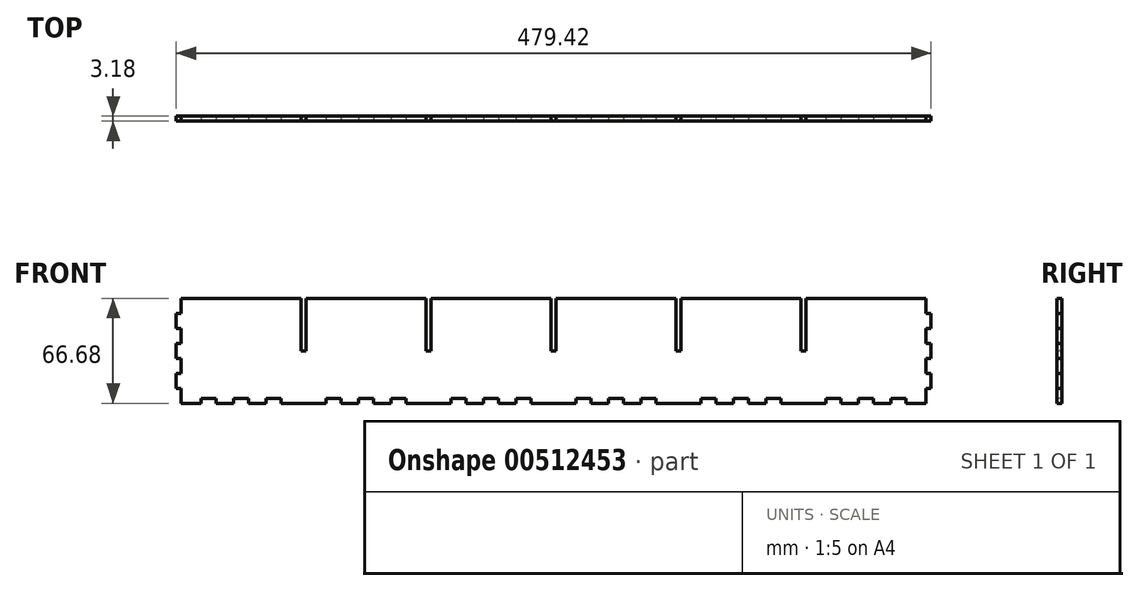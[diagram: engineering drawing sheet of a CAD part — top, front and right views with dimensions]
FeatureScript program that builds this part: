
annotation { "Feature Type Name" : "Feature", "Feature Type Description" : "" }
export const myFeature = defineFeature(function(context is Context, id is Id, definition is map)
    precondition{}
    {
        {
            var Q0;
            Q0=qCreatedBy(makeId("Front.planeOp"),FACE);
            var sketch = newSketch(context, id + "F0", { "sketchPlane" : qUnion([Q0])});
            skLineSegment(sketch, "E0.bottom", {"start": v(-239.71, 33.34) * mm, "end": v(239.71, 33.34) * mm});
            skLineSegment(sketch, "E0.top", {"start": v(-239.71, -33.34) * mm, "end": v(239.71, -33.34) * mm});
            skLineSegment(sketch, "E0.left", {"start": v(-239.71, 33.34) * mm, "end": v(-239.71, -33.34) * mm});
            skLineSegment(sketch, "E0.right", {"start": v(239.71, 33.34) * mm, "end": v(239.71, -33.34) * mm});
            skSolve(sketch);
        }
        {
            var Q0;
            Q0=makeQuery(id+"F0.imprint","IMPRINT",FACE,{"disambiguationData":[TD([[makeQuery(id+"F0.imprint","IMPRINT",EDGE,{"derivedFrom":sQuery(id+"F0.wireOp",EDGE,"E0.bottom")}),-1.0]])]});
            extrude(context, id + "F1", {"entities" : qUnion([Q0]), "depth" : 3.17 * mm});
        }
        {
            var Q0;
            Q0=makeQuery(id+"F1.opExtrude","CAP_FACE",FACE,{"disambiguationData":[OSD([sQuery(id+"F0.wireOp",EDGE,"E0.bottom"),sQuery(id+"F0.wireOp",EDGE,"E0.top"),sQuery(id+"F0.wireOp",EDGE,"E0.left"),sQuery(id+"F0.wireOp",EDGE,"E0.right")])],"isStart":false});
            var sketch = newSketch(context, id + "F2", { "sketchPlane" : qUnion([Q0])});
            skLineSegment(sketch, "E1.bottom", {"start": v(-239.71, -33.34) * mm, "end": v(-236.54, -33.34) * mm});
            skLineSegment(sketch, "E1.top", {"start": v(-239.71, -23.81) * mm, "end": v(-236.54, -23.81) * mm});
            skLineSegment(sketch, "E1.left", {"start": v(-239.71, -33.34) * mm, "end": v(-239.71, -23.81) * mm});
            skLineSegment(sketch, "E1.right", {"start": v(-236.54, -33.34) * mm, "end": v(-236.54, -23.81) * mm});
            skLineSegment(sketch, "E2.0.1.0", {"start": v(-236.54, -14.29) * mm, "end": v(-236.54, -4.76) * mm});
            skLineSegment(sketch, "E2.0.1.1", {"start": v(-239.71, -14.29) * mm, "end": v(-239.71, -4.76) * mm});
            skLineSegment(sketch, "E2.0.1.2", {"start": v(-239.71, -4.76) * mm, "end": v(-236.54, -4.76) * mm});
            skLineSegment(sketch, "E2.0.1.3", {"start": v(-239.71, -14.29) * mm, "end": v(-236.54, -14.29) * mm});
            skLineSegment(sketch, "E2.0.2.0", {"start": v(-236.54, 4.76) * mm, "end": v(-236.54, 14.29) * mm});
            skLineSegment(sketch, "E2.0.2.1", {"start": v(-239.71, 4.76) * mm, "end": v(-239.71, 14.29) * mm});
            skLineSegment(sketch, "E2.0.2.2", {"start": v(-239.71, 14.29) * mm, "end": v(-236.54, 14.29) * mm});
            skLineSegment(sketch, "E2.0.2.3", {"start": v(-239.71, 4.76) * mm, "end": v(-236.54, 4.76) * mm});
            skLineSegment(sketch, "E2.0.3.0", {"start": v(-236.54, 23.81) * mm, "end": v(-236.54, 33.34) * mm});
            skLineSegment(sketch, "E2.0.3.1", {"start": v(-239.71, 23.81) * mm, "end": v(-239.71, 33.34) * mm});
            skLineSegment(sketch, "E2.0.3.2", {"start": v(-239.71, 33.34) * mm, "end": v(-236.54, 33.34) * mm});
            skLineSegment(sketch, "E2.0.3.3", {"start": v(-239.71, 23.81) * mm, "end": v(-236.54, 23.81) * mm});
            skLineSegment(sketch, "E2.1.0.0", {"start": v(239.71, -33.34) * mm, "end": v(239.71, -23.81) * mm});
            skLineSegment(sketch, "E2.1.0.1", {"start": v(236.54, -33.34) * mm, "end": v(236.54, -23.81) * mm});
            skLineSegment(sketch, "E2.1.0.2", {"start": v(236.54, -23.81) * mm, "end": v(239.71, -23.81) * mm});
            skLineSegment(sketch, "E2.1.0.3", {"start": v(236.54, -33.34) * mm, "end": v(239.71, -33.34) * mm});
            skLineSegment(sketch, "E2.1.1.0", {"start": v(239.71, -14.29) * mm, "end": v(239.71, -4.76) * mm});
            skLineSegment(sketch, "E2.1.1.1", {"start": v(236.54, -14.29) * mm, "end": v(236.54, -4.76) * mm});
            skLineSegment(sketch, "E2.1.1.2", {"start": v(236.54, -4.76) * mm, "end": v(239.71, -4.76) * mm});
            skLineSegment(sketch, "E2.1.1.3", {"start": v(236.54, -14.29) * mm, "end": v(239.71, -14.29) * mm});
            skLineSegment(sketch, "E2.1.2.0", {"start": v(239.71, 4.76) * mm, "end": v(239.71, 14.29) * mm});
            skLineSegment(sketch, "E2.1.2.1", {"start": v(236.54, 4.76) * mm, "end": v(236.54, 14.29) * mm});
            skLineSegment(sketch, "E2.1.2.2", {"start": v(236.54, 14.29) * mm, "end": v(239.71, 14.29) * mm});
            skLineSegment(sketch, "E2.1.2.3", {"start": v(236.54, 4.76) * mm, "end": v(239.71, 4.76) * mm});
            skLineSegment(sketch, "E2.1.3.0", {"start": v(239.71, 23.81) * mm, "end": v(239.71, 33.34) * mm});
            skLineSegment(sketch, "E2.1.3.1", {"start": v(236.54, 23.81) * mm, "end": v(236.54, 33.34) * mm});
            skLineSegment(sketch, "E2.1.3.2", {"start": v(236.54, 33.34) * mm, "end": v(239.71, 33.34) * mm});
            skLineSegment(sketch, "E2.1.3.3", {"start": v(236.54, 23.81) * mm, "end": v(239.71, 23.81) * mm});
            skLineSegment(sketch, "E2.direction1", {"start": v(-239.71, -33.34) * mm, "end": v(236.54, -33.34) * mm, "construction": true});
            skLineSegment(sketch, "E2.direction2", {"start": v(-239.71, -33.34) * mm, "end": v(-239.71, -14.29) * mm, "construction": true});
            skSolve(sketch);
        }
        {
            var Q0;
            Q0=qSketchRegion(id+"F2",true);
            extrude(context, id + "F3", {"entities" : qUnion([Q0]), "operationType" : NewBodyOperationType.REMOVE, "endBound" : BoundingType.THROUGH_ALL, "oppositeDirection" : true, "depth" : 25.4 * mm});
        }
        {
            var Q0;
            Q0=makeQuery(id+"F1.opExtrude","CAP_FACE",FACE,{"disambiguationData":[OSD([sQuery(id+"F0.wireOp",EDGE,"E0.bottom"),sQuery(id+"F0.wireOp",EDGE,"E0.top"),sQuery(id+"F0.wireOp",EDGE,"E0.left"),sQuery(id+"F0.wireOp",EDGE,"E0.right")])],"isStart":false});
            var sketch = newSketch(context, id + "F4", { "sketchPlane" : qUnion([Q0])});
            skLineSegment(sketch, "E3.bottom", {"start": v(-160.34, 33.34) * mm, "end": v(-157.16, 33.34) * mm});
            skLineSegment(sketch, "E3.top", {"start": v(-160.34, 0) * mm, "end": v(-157.16, 0) * mm});
            skLineSegment(sketch, "E3.left", {"start": v(-160.34, 33.34) * mm, "end": v(-160.34, 0) * mm});
            skLineSegment(sketch, "E3.right", {"start": v(-157.16, 33.34) * mm, "end": v(-157.16, 0) * mm});
            skLineSegment(sketch, "E4.1.0.0", {"start": v(-80.96, 33.34) * mm, "end": v(-80.96, 0) * mm});
            skLineSegment(sketch, "E4.1.0.1", {"start": v(-77.79, 33.34) * mm, "end": v(-77.79, 0) * mm});
            skLineSegment(sketch, "E4.1.0.2", {"start": v(-80.96, 33.34) * mm, "end": v(-77.79, 33.34) * mm});
            skLineSegment(sketch, "E4.1.0.3", {"start": v(-80.96, 0) * mm, "end": v(-77.79, 0) * mm});
            skLineSegment(sketch, "E4.2.0.0", {"start": v(-1.59, 33.34) * mm, "end": v(-1.59, 0) * mm});
            skLineSegment(sketch, "E4.2.0.1", {"start": v(1.59, 33.34) * mm, "end": v(1.59, 0) * mm});
            skLineSegment(sketch, "E4.2.0.2", {"start": v(-1.59, 33.34) * mm, "end": v(1.59, 33.34) * mm});
            skLineSegment(sketch, "E4.2.0.3", {"start": v(-1.59, 0) * mm, "end": v(1.59, 0) * mm});
            skLineSegment(sketch, "E4.3.0.0", {"start": v(77.79, 33.34) * mm, "end": v(77.79, 0) * mm});
            skLineSegment(sketch, "E4.3.0.1", {"start": v(80.96, 33.34) * mm, "end": v(80.96, 0) * mm});
            skLineSegment(sketch, "E4.3.0.2", {"start": v(77.79, 33.34) * mm, "end": v(80.96, 33.34) * mm});
            skLineSegment(sketch, "E4.3.0.3", {"start": v(77.79, 0) * mm, "end": v(80.96, 0) * mm});
            skLineSegment(sketch, "E4.4.0.0", {"start": v(157.16, 33.34) * mm, "end": v(157.16, 0) * mm});
            skLineSegment(sketch, "E4.4.0.1", {"start": v(160.34, 33.34) * mm, "end": v(160.34, 0) * mm});
            skLineSegment(sketch, "E4.4.0.2", {"start": v(157.16, 33.34) * mm, "end": v(160.34, 33.34) * mm});
            skLineSegment(sketch, "E4.4.0.3", {"start": v(157.16, 0) * mm, "end": v(160.34, 0) * mm});
            skLineSegment(sketch, "E4.direction1", {"start": v(-160.34, 0) * mm, "end": v(-80.96, 0) * mm, "construction": true});
            skSolve(sketch);
        }
        {
            var Q0;
            Q0 = qSketchRegion(id + "F4", true);
            extrude(context, id + "F5", {"entities" : qUnion([Q0]), "operationType" : NewBodyOperationType.REMOVE, "endBound" : BoundingType.THROUGH_ALL, "oppositeDirection" : true, "depth" : 25.4 * mm});
        }
        {
            var Q0;
            Q0=makeQuery(id+"F1.opExtrude","CAP_FACE",FACE,{"disambiguationData":[OSD([sQuery(id+"F0.wireOp",EDGE,"E0.bottom"),sQuery(id+"F0.wireOp",EDGE,"E0.top"),sQuery(id+"F0.wireOp",EDGE,"E0.left"),sQuery(id+"F0.wireOp",EDGE,"E0.right")])],"isStart":false});
            var sketch = newSketch(context, id + "F6", { "sketchPlane" : qUnion([Q0])});
            skLineSegment(sketch, "E5.bottom", {"start": v(-223.84, -33.34) * mm, "end": v(-214.31, -33.34) * mm});
            skLineSegment(sketch, "E5.top", {"start": v(-223.84, -30.16) * mm, "end": v(-214.31, -30.16) * mm});
            skLineSegment(sketch, "E5.left", {"start": v(-223.84, -33.34) * mm, "end": v(-223.84, -30.16) * mm});
            skLineSegment(sketch, "E5.right", {"start": v(-214.31, -33.34) * mm, "end": v(-214.31, -30.16) * mm});
            skLineSegment(sketch, "E6.1.0.0", {"start": v(-203.2, -30.16) * mm, "end": v(-193.68, -30.16) * mm});
            skLineSegment(sketch, "E6.1.0.1", {"start": v(-203.2, -33.34) * mm, "end": v(-193.68, -33.34) * mm});
            skLineSegment(sketch, "E6.1.0.2", {"start": v(-203.2, -33.34) * mm, "end": v(-203.2, -30.16) * mm});
            skLineSegment(sketch, "E6.1.0.3", {"start": v(-193.68, -33.34) * mm, "end": v(-193.68, -30.16) * mm});
            skLineSegment(sketch, "E6.2.0.0", {"start": v(-182.56, -30.16) * mm, "end": v(-173.04, -30.16) * mm});
            skLineSegment(sketch, "E6.2.0.1", {"start": v(-182.56, -33.34) * mm, "end": v(-173.04, -33.34) * mm});
            skLineSegment(sketch, "E6.2.0.2", {"start": v(-182.56, -33.34) * mm, "end": v(-182.56, -30.16) * mm});
            skLineSegment(sketch, "E6.2.0.3", {"start": v(-173.04, -33.34) * mm, "end": v(-173.04, -30.16) * mm});
            skLineSegment(sketch, "E6.direction1", {"start": v(-223.84, -33.34) * mm, "end": v(-203.2, -33.34) * mm, "construction": true});
            skLineSegment(sketch, "E7.1.0.0", {"start": v(-144.46, -30.16) * mm, "end": v(-134.94, -30.16) * mm});
            skLineSegment(sketch, "E7.1.0.1", {"start": v(-144.46, -33.34) * mm, "end": v(-123.83, -33.34) * mm, "construction": true});
            skLineSegment(sketch, "E7.1.0.2", {"start": v(-123.83, -30.16) * mm, "end": v(-114.3, -30.16) * mm});
            skLineSegment(sketch, "E7.1.0.3", {"start": v(-103.19, -33.34) * mm, "end": v(-93.66, -33.34) * mm});
            skLineSegment(sketch, "E7.1.0.4", {"start": v(-123.83, -33.34) * mm, "end": v(-114.3, -33.34) * mm});
            skLineSegment(sketch, "E7.1.0.5", {"start": v(-103.19, -30.16) * mm, "end": v(-93.66, -30.16) * mm});
            skLineSegment(sketch, "E7.1.0.6", {"start": v(-144.46, -33.34) * mm, "end": v(-134.94, -33.34) * mm});
            skLineSegment(sketch, "E7.1.0.7", {"start": v(-134.94, -33.34) * mm, "end": v(-134.94, -30.16) * mm});
            skLineSegment(sketch, "E7.1.0.8", {"start": v(-144.46, -33.34) * mm, "end": v(-144.46, -30.16) * mm});
            skLineSegment(sketch, "E7.1.0.9", {"start": v(-123.83, -33.34) * mm, "end": v(-123.83, -30.16) * mm});
            skLineSegment(sketch, "E7.1.0.10", {"start": v(-93.66, -33.34) * mm, "end": v(-93.66, -30.16) * mm});
            skLineSegment(sketch, "E7.1.0.11", {"start": v(-114.3, -33.34) * mm, "end": v(-114.3, -30.16) * mm});
            skLineSegment(sketch, "E7.1.0.12", {"start": v(-103.19, -33.34) * mm, "end": v(-103.19, -30.16) * mm});
            skLineSegment(sketch, "E7.2.0.0", {"start": v(-65.09, -30.16) * mm, "end": v(-55.56, -30.16) * mm});
            skLineSegment(sketch, "E7.2.0.1", {"start": v(-65.09, -33.34) * mm, "end": v(-44.45, -33.34) * mm, "construction": true});
            skLineSegment(sketch, "E7.2.0.2", {"start": v(-44.45, -30.16) * mm, "end": v(-34.93, -30.16) * mm});
            skLineSegment(sketch, "E7.2.0.3", {"start": v(-23.81, -33.34) * mm, "end": v(-14.29, -33.34) * mm});
            skLineSegment(sketch, "E7.2.0.4", {"start": v(-44.45, -33.34) * mm, "end": v(-34.93, -33.34) * mm});
            skLineSegment(sketch, "E7.2.0.5", {"start": v(-23.81, -30.16) * mm, "end": v(-14.29, -30.16) * mm});
            skLineSegment(sketch, "E7.2.0.6", {"start": v(-65.09, -33.34) * mm, "end": v(-55.56, -33.34) * mm});
            skLineSegment(sketch, "E7.2.0.7", {"start": v(-55.56, -33.34) * mm, "end": v(-55.56, -30.16) * mm});
            skLineSegment(sketch, "E7.2.0.8", {"start": v(-65.09, -33.34) * mm, "end": v(-65.09, -30.16) * mm});
            skLineSegment(sketch, "E7.2.0.9", {"start": v(-44.45, -33.34) * mm, "end": v(-44.45, -30.16) * mm});
            skLineSegment(sketch, "E7.2.0.10", {"start": v(-14.29, -33.34) * mm, "end": v(-14.29, -30.16) * mm});
            skLineSegment(sketch, "E7.2.0.11", {"start": v(-34.93, -33.34) * mm, "end": v(-34.93, -30.16) * mm});
            skLineSegment(sketch, "E7.2.0.12", {"start": v(-23.81, -33.34) * mm, "end": v(-23.81, -30.16) * mm});
            skLineSegment(sketch, "E7.3.0.0", {"start": v(14.29, -30.16) * mm, "end": v(23.81, -30.16) * mm});
            skLineSegment(sketch, "E7.3.0.1", {"start": v(14.29, -33.34) * mm, "end": v(34.92, -33.34) * mm, "construction": true});
            skLineSegment(sketch, "E7.3.0.2", {"start": v(34.92, -30.16) * mm, "end": v(44.45, -30.16) * mm});
            skLineSegment(sketch, "E7.3.0.3", {"start": v(55.56, -33.34) * mm, "end": v(65.09, -33.34) * mm});
            skLineSegment(sketch, "E7.3.0.4", {"start": v(34.92, -33.34) * mm, "end": v(44.45, -33.34) * mm});
            skLineSegment(sketch, "E7.3.0.5", {"start": v(55.56, -30.16) * mm, "end": v(65.09, -30.16) * mm});
            skLineSegment(sketch, "E7.3.0.6", {"start": v(14.29, -33.34) * mm, "end": v(23.81, -33.34) * mm});
            skLineSegment(sketch, "E7.3.0.7", {"start": v(23.81, -33.34) * mm, "end": v(23.81, -30.16) * mm});
            skLineSegment(sketch, "E7.3.0.8", {"start": v(14.29, -33.34) * mm, "end": v(14.29, -30.16) * mm});
            skLineSegment(sketch, "E7.3.0.9", {"start": v(34.92, -33.34) * mm, "end": v(34.92, -30.16) * mm});
            skLineSegment(sketch, "E7.3.0.10", {"start": v(65.09, -33.34) * mm, "end": v(65.09, -30.16) * mm});
            skLineSegment(sketch, "E7.3.0.11", {"start": v(44.45, -33.34) * mm, "end": v(44.45, -30.16) * mm});
            skLineSegment(sketch, "E7.3.0.12", {"start": v(55.56, -33.34) * mm, "end": v(55.56, -30.16) * mm});
            skLineSegment(sketch, "E7.4.0.0", {"start": v(93.66, -30.16) * mm, "end": v(103.19, -30.16) * mm});
            skLineSegment(sketch, "E7.4.0.1", {"start": v(93.66, -33.34) * mm, "end": v(114.3, -33.34) * mm, "construction": true});
            skLineSegment(sketch, "E7.4.0.2", {"start": v(114.3, -30.16) * mm, "end": v(123.82, -30.16) * mm});
            skLineSegment(sketch, "E7.4.0.3", {"start": v(134.94, -33.34) * mm, "end": v(144.46, -33.34) * mm});
            skLineSegment(sketch, "E7.4.0.4", {"start": v(114.3, -33.34) * mm, "end": v(123.82, -33.34) * mm});
            skLineSegment(sketch, "E7.4.0.5", {"start": v(134.94, -30.16) * mm, "end": v(144.46, -30.16) * mm});
            skLineSegment(sketch, "E7.4.0.6", {"start": v(93.66, -33.34) * mm, "end": v(103.19, -33.34) * mm});
            skLineSegment(sketch, "E7.4.0.7", {"start": v(103.19, -33.34) * mm, "end": v(103.19, -30.16) * mm});
            skLineSegment(sketch, "E7.4.0.8", {"start": v(93.66, -33.34) * mm, "end": v(93.66, -30.16) * mm});
            skLineSegment(sketch, "E7.4.0.9", {"start": v(114.3, -33.34) * mm, "end": v(114.3, -30.16) * mm});
            skLineSegment(sketch, "E7.4.0.10", {"start": v(144.46, -33.34) * mm, "end": v(144.46, -30.16) * mm});
            skLineSegment(sketch, "E7.4.0.11", {"start": v(123.82, -33.34) * mm, "end": v(123.82, -30.16) * mm});
            skLineSegment(sketch, "E7.4.0.12", {"start": v(134.94, -33.34) * mm, "end": v(134.94, -30.16) * mm});
            skLineSegment(sketch, "E7.5.0.0", {"start": v(173.04, -30.16) * mm, "end": v(182.56, -30.16) * mm});
            skLineSegment(sketch, "E7.5.0.1", {"start": v(173.04, -33.34) * mm, "end": v(193.67, -33.34) * mm, "construction": true});
            skLineSegment(sketch, "E7.5.0.2", {"start": v(193.67, -30.16) * mm, "end": v(203.2, -30.16) * mm});
            skLineSegment(sketch, "E7.5.0.3", {"start": v(214.31, -33.34) * mm, "end": v(223.84, -33.34) * mm});
            skLineSegment(sketch, "E7.5.0.4", {"start": v(193.67, -33.34) * mm, "end": v(203.2, -33.34) * mm});
            skLineSegment(sketch, "E7.5.0.5", {"start": v(214.31, -30.16) * mm, "end": v(223.84, -30.16) * mm});
            skLineSegment(sketch, "E7.5.0.6", {"start": v(173.04, -33.34) * mm, "end": v(182.56, -33.34) * mm});
            skLineSegment(sketch, "E7.5.0.7", {"start": v(182.56, -33.34) * mm, "end": v(182.56, -30.16) * mm});
            skLineSegment(sketch, "E7.5.0.8", {"start": v(173.04, -33.34) * mm, "end": v(173.04, -30.16) * mm});
            skLineSegment(sketch, "E7.5.0.9", {"start": v(193.67, -33.34) * mm, "end": v(193.67, -30.16) * mm});
            skLineSegment(sketch, "E7.5.0.10", {"start": v(223.84, -33.34) * mm, "end": v(223.84, -30.16) * mm});
            skLineSegment(sketch, "E7.5.0.11", {"start": v(203.2, -33.34) * mm, "end": v(203.2, -30.16) * mm});
            skLineSegment(sketch, "E7.5.0.12", {"start": v(214.31, -33.34) * mm, "end": v(214.31, -30.16) * mm});
            skLineSegment(sketch, "E7.direction1", {"start": v(-223.84, -33.34) * mm, "end": v(-144.46, -33.34) * mm, "construction": true});
            skSolve(sketch);
        }
        {
            var Q0;
            Q0 = qSketchRegion(id + "F6", true);
            extrude(context, id + "F7", {"entities" : qUnion([Q0]), "operationType" : NewBodyOperationType.REMOVE, "endBound" : BoundingType.THROUGH_ALL, "oppositeDirection" : true, "depth" : 25.4 * mm});
        }
    });
